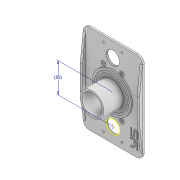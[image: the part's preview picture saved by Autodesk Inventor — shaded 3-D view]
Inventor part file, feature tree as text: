
AUTODESK INVENTOR PART (.ipt)
format: ipt  version: 2020.3 (Build 243373000, 373)  size: 308,736 bytes
history: native  units: mm
features: sketch x3, extrude x2, imported_body x1
ambient origin geometry x8: Origin, YZ Plane, XZ Plane, XY Plane, X Axis, Y Axis, Z Axis, Center Point
bodies: Solid1 (feature_tree)
feature tree (6):
  extrude  "Extrusion1"  Depth=1.0mm TaperAngle=0.0deg
  extrude  "Extrusion2"  [1 undecoded]
  sketch  "Sketch3"
  sketch  "Sketch1"  dims[d0=1.0mm d1=0.0mm d2=1.0mm d3=0.0mm]
  sketch  "Sketch2"  dims[d4=50.0mm]
  imported_body  "Base1"
note: 1 required parameter value undecoded (feature->parameter linkage not recoverable at this tier; creation-order binding heuristic only, values carry confidence <= 0.55)
